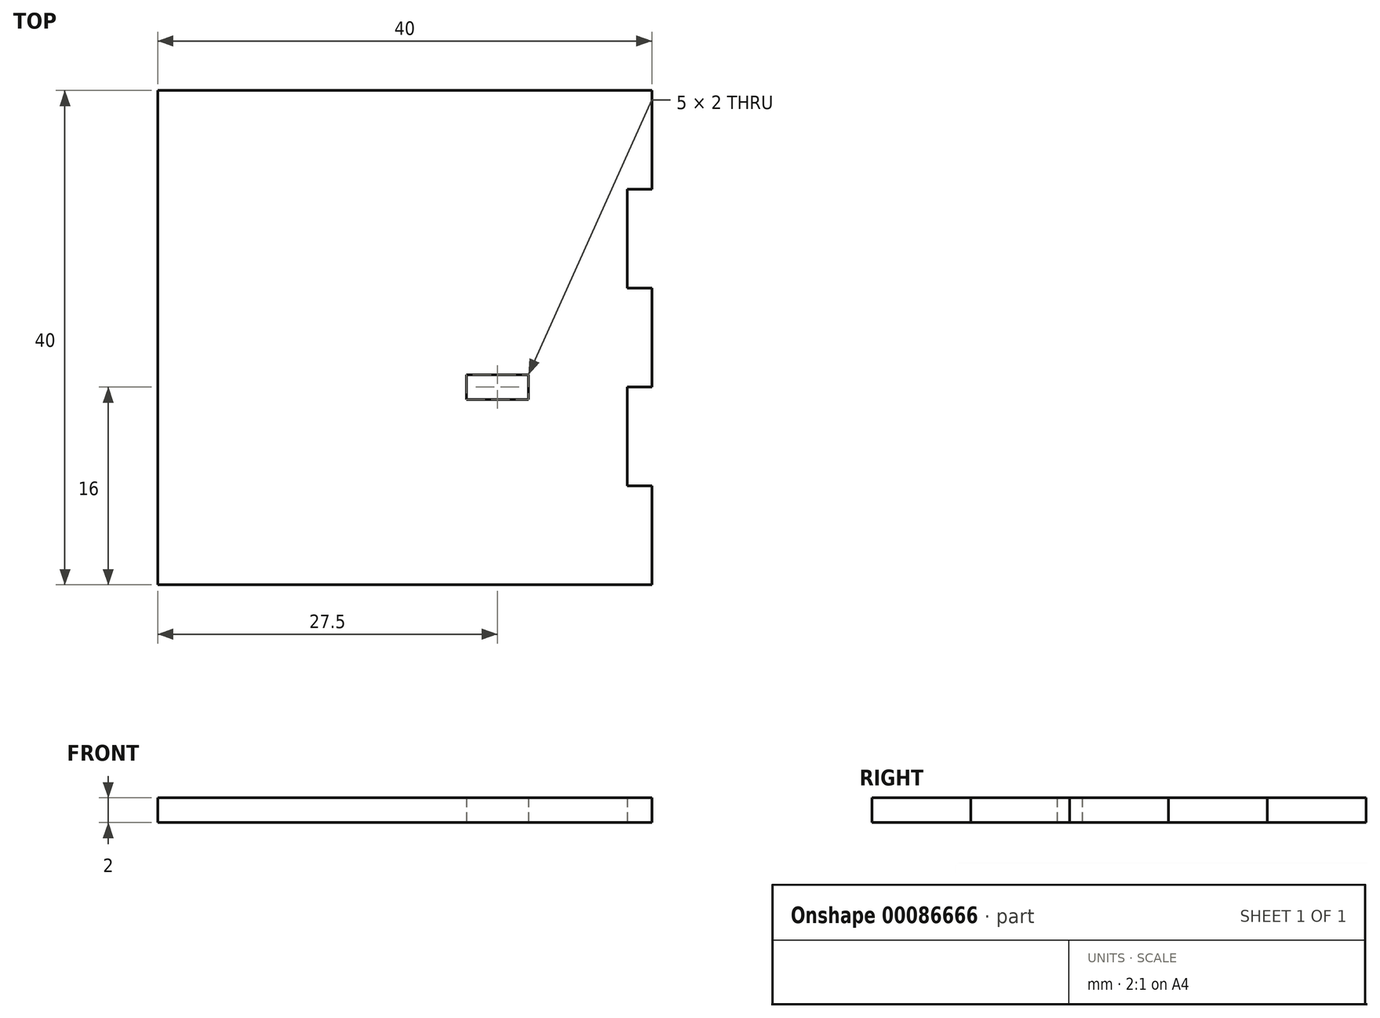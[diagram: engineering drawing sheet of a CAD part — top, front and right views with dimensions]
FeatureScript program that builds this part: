
annotation { "Feature Type Name" : "Feature", "Feature Type Description" : "" }
export const myFeature = defineFeature(function(context is Context, id is Id, definition is map)
    precondition{}
    {
        {
            var Q0;
            Q0=qCreatedBy(makeId("Top.planeOp"),FACE);
            var sketch = newSketch(context, id + "F2", { "sketchPlane" : qUnion([Q0])});
            skLineSegment(sketch, "E0", {"start": v(2, 0) * mm, "end": v(42, 0) * mm});
            skLineSegment(sketch, "E1", {"start": v(42, 0) * mm, "end": v(42, 8) * mm});
            skLineSegment(sketch, "E2", {"start": v(42, 8) * mm, "end": v(40, 8) * mm});
            skLineSegment(sketch, "E3", {"start": v(40, 8) * mm, "end": v(40, 16) * mm});
            skLineSegment(sketch, "E4", {"start": v(40, 16) * mm, "end": v(42, 16) * mm});
            skLineSegment(sketch, "E5", {"start": v(42, 16) * mm, "end": v(42, 24) * mm});
            skLineSegment(sketch, "E6", {"start": v(42, 24) * mm, "end": v(40, 24) * mm});
            skLineSegment(sketch, "E7", {"start": v(40, 24) * mm, "end": v(40, 32) * mm});
            skLineSegment(sketch, "E8", {"start": v(40, 32) * mm, "end": v(42, 32) * mm});
            skLineSegment(sketch, "E9", {"start": v(42, 32) * mm, "end": v(42, 40) * mm});
            skLineSegment(sketch, "E10", {"start": v(42, 40) * mm, "end": v(2, 40) * mm});
            skLineSegment(sketch, "E11", {"start": v(2, 40) * mm, "end": v(2, 0) * mm});
            skSolve(sketch);
        }
        {
            var Q0;
            Q0=makeQuery(id+"F2.imprint","IMPRINT",FACE,{"disambiguationData":[TD([[makeQuery(id+"F2.imprint","IMPRINT",EDGE,{"derivedFrom":sQuery(id+"F2.wireOp",EDGE,"9986847f-93a7-40bd-9da1-1ac629096ef9")}),1.0]])]});
            var Q1;
            Q1=makeQuery(id+"F2.imprint","IMPRINT",FACE,{"disambiguationData":[TD([[makeQuery(id+"F2.imprint","IMPRINT",EDGE,{"derivedFrom":sQuery(id+"F2.wireOp",EDGE,"E0")}),1.0]])]});
            var Q2;
            Q2=makeQuery(id+"F2.imprint","IMPRINT",FACE,{"disambiguationData":[TD([[makeQuery(id+"F2.imprint","IMPRINT",EDGE,{"derivedFrom":sQuery(id+"F2.wireOp",EDGE,"e620274a-1ef1-4e1f-b964-3f320ad0e6cd")}),1.0]])]});
            var Q3;
            Q3=makeQuery(id+"F2.imprint","IMPRINT",FACE,{"disambiguationData":[TD([[makeQuery(id+"F2.imprint","IMPRINT",EDGE,{"derivedFrom":sQuery(id+"F2.wireOp",EDGE,"570af66b-53b3-47f8-9f40-16c496dc11be")}),-1.0]])]});
            extrude(context, id + "F0", {"entities" : qUnion([Q0, Q1, Q2, Q3]), "depth" : 2 * mm});
        }
        {
            var Q0;
            Q0=qCreatedBy(makeId("Top.planeOp"),FACE);
            var sketch = newSketch(context, id + "F1", { "sketchPlane" : qUnion([Q0])});
            skLineSegment(sketch, "E12.bottom", {"start": v(27, 17) * mm, "end": v(32, 17) * mm});
            skLineSegment(sketch, "E12.top", {"start": v(27, 15) * mm, "end": v(32, 15) * mm});
            skLineSegment(sketch, "E12.left", {"start": v(27, 17) * mm, "end": v(27, 15) * mm});
            skLineSegment(sketch, "E12.right", {"start": v(32, 17) * mm, "end": v(32, 15) * mm});
            skSolve(sketch);
        }
        {
            var Q0;
            Q0=makeQuery(id+"F1.imprint","IMPRINT",FACE,{"disambiguationData":[TD([[makeQuery(id+"F1.imprint","IMPRINT",EDGE,{"derivedFrom":sQuery(id+"F1.wireOp",EDGE,"E12.bottom")}),-1.0]])]});
            extrude(context, id + "F3", {"entities" : qUnion([Q0]), "operationType" : NewBodyOperationType.REMOVE, "depth" : 2 * mm});
        }
    });
